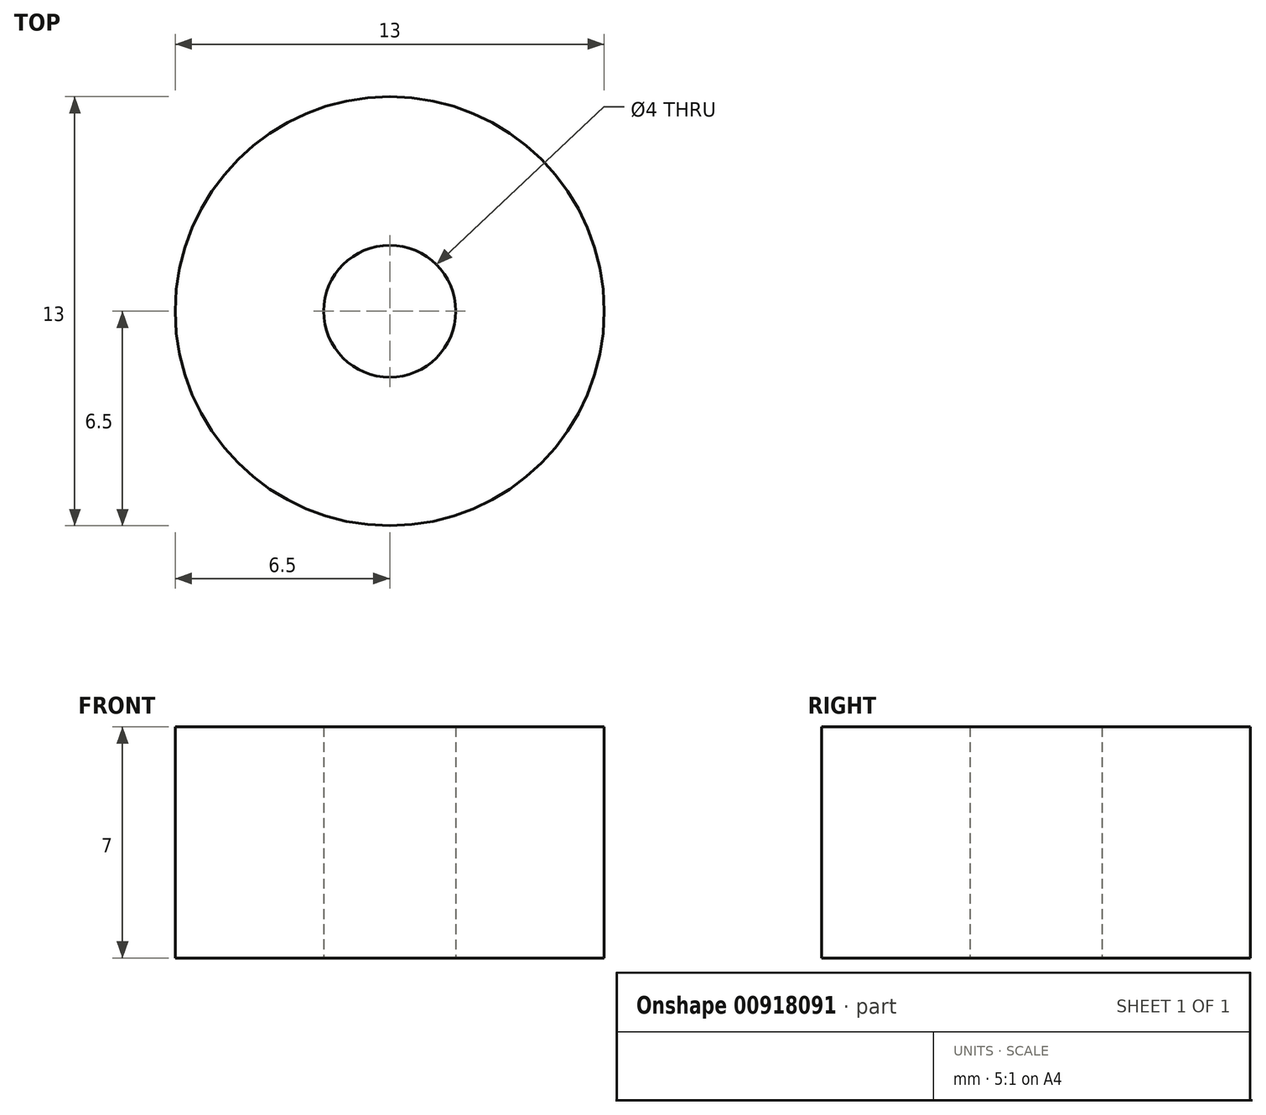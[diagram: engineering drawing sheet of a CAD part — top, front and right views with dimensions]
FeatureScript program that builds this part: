
annotation { "Feature Type Name" : "Feature", "Feature Type Description" : "" }
export const myFeature = defineFeature(function(context is Context, id is Id, definition is map)
    precondition{}
    {
        {
            var Q0;
            Q0=qCreatedBy(makeId("Top.planeOp"),FACE);
            var sketch = newSketch(context, id + "F0", { "sketchPlane" : qUnion([Q0])});
            skCircle(sketch, "E0", {"center": v(0, 0) * mm, "radius": 6.5 * mm});
            skCircle(sketch, "E1", {"center": v(0, 0) * mm, "radius": 2 * mm});
            skSolve(sketch);
        }
        {
            var Q0;
            Q0=qSketchRegion(id+"F0",true);
            extrude(context, id + "F1", {"entities" : qUnion([Q0]), "depth" : 7 * mm});
        }
    });
